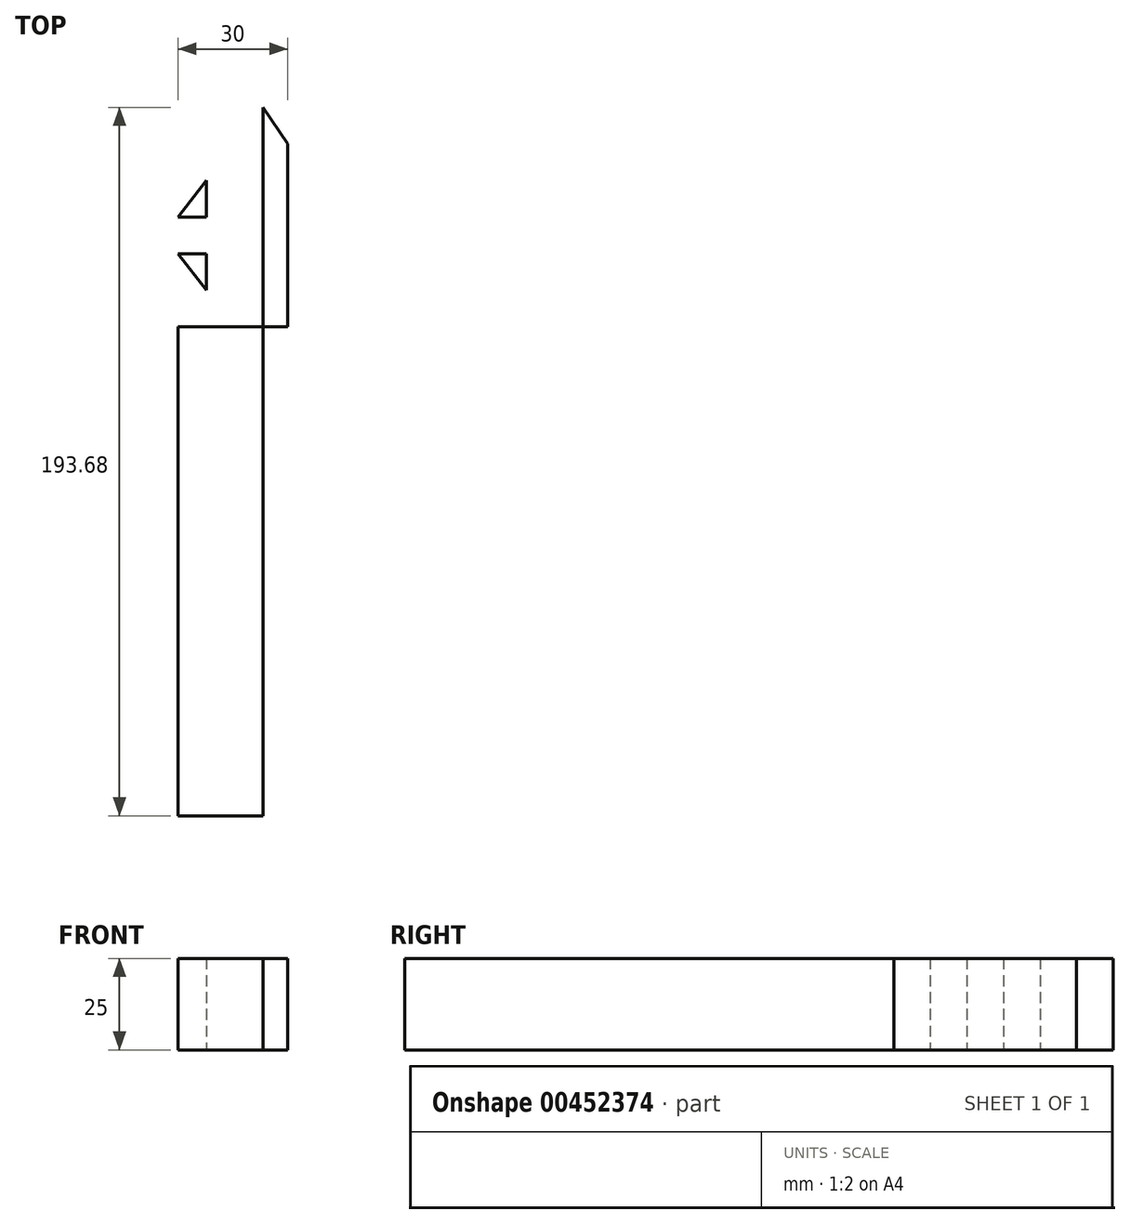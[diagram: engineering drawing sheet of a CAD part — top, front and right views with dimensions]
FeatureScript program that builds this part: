
annotation { "Feature Type Name" : "Feature", "Feature Type Description" : "" }
export const myFeature = defineFeature(function(context is Context, id is Id, definition is map)
    precondition{}
    {
        {
            var Q0;
            Q0=qCreatedBy(makeId("Top.planeOp"),FACE);
            var sketch = newSketch(context, id + "F0", { "sketchPlane" : qUnion([Q0])});
            skLineSegment(sketch, "E0.bottom", {"start": v(-3.87, -96.84) * mm, "end": v(3.87, -96.84) * mm});
            skLineSegment(sketch, "E0.top", {"start": v(-3.87, 96.84) * mm, "end": v(3.87, 96.84) * mm});
            skLineSegment(sketch, "E0.left", {"start": v(-3.87, -96.84) * mm, "end": v(-3.87, 96.84) * mm});
            skLineSegment(sketch, "E0.right", {"start": v(3.87, -96.84) * mm, "end": v(3.87, 96.84) * mm});
            skPoint(sketch, "E0.middle", {"position": v(0, 0) * mm});
            skLineSegment(sketch, "E1.bottom", {"start": v(-3.87, 96.84) * mm, "end": v(-11.62, 96.84) * mm});
            skLineSegment(sketch, "E1.top", {"start": v(-3.87, -96.84) * mm, "end": v(-11.62, -96.84) * mm});
            skLineSegment(sketch, "E1.left", {"start": v(-3.87, 96.84) * mm, "end": v(-3.87, -96.84) * mm});
            skLineSegment(sketch, "E1.right", {"start": v(-11.62, 96.84) * mm, "end": v(-11.62, -96.84) * mm});
            skLineSegment(sketch, "E2.bottom", {"start": v(3.87, -96.84) * mm, "end": v(11.62, -96.84) * mm});
            skLineSegment(sketch, "E2.top", {"start": v(3.87, 96.84) * mm, "end": v(11.62, 96.84) * mm});
            skLineSegment(sketch, "E2.right", {"start": v(11.62, -96.84) * mm, "end": v(11.62, 96.84) * mm});
            skLineSegment(sketch, "E3.bottom", {"start": v(-11.62, 96.84) * mm, "end": v(18.38, 96.84) * mm});
            skLineSegment(sketch, "E3.top", {"start": v(-11.62, 86.84) * mm, "end": v(18.38, 86.84) * mm});
            skLineSegment(sketch, "E3.left", {"start": v(-11.62, 96.84) * mm, "end": v(-11.62, 86.84) * mm});
            skLineSegment(sketch, "E3.right", {"start": v(18.38, 96.84) * mm, "end": v(18.38, 86.84) * mm});
            skLineSegment(sketch, "E4.top", {"start": v(-11.62, 76.84) * mm, "end": v(18.38, 76.84) * mm});
            skLineSegment(sketch, "E4.left", {"start": v(-11.62, 86.84) * mm, "end": v(-11.62, 76.84) * mm});
            skLineSegment(sketch, "E4.right", {"start": v(18.38, 86.84) * mm, "end": v(18.38, 76.84) * mm});
            skLineSegment(sketch, "E5.top", {"start": v(-11.62, 66.84) * mm, "end": v(18.38, 66.84) * mm});
            skLineSegment(sketch, "E5.left", {"start": v(-11.62, 76.84) * mm, "end": v(-11.62, 66.84) * mm});
            skLineSegment(sketch, "E5.right", {"start": v(18.38, 76.84) * mm, "end": v(18.38, 66.84) * mm});
            skLineSegment(sketch, "E6.top", {"start": v(-11.62, 56.84) * mm, "end": v(18.38, 56.84) * mm});
            skLineSegment(sketch, "E6.left", {"start": v(-11.62, 66.84) * mm, "end": v(-11.62, 56.84) * mm});
            skLineSegment(sketch, "E6.right", {"start": v(18.38, 66.84) * mm, "end": v(18.38, 56.84) * mm});
            skLineSegment(sketch, "E7.bottom", {"start": v(-11.62, 56.84) * mm, "end": v(8.73, 56.84) * mm});
            skLineSegment(sketch, "E7.top", {"start": v(-11.62, 46.84) * mm, "end": v(8.73, 46.84) * mm});
            skLineSegment(sketch, "E7.left", {"start": v(-11.62, 56.84) * mm, "end": v(-11.62, 46.84) * mm});
            skLineSegment(sketch, "E8.bottom", {"start": v(-11.62, 46.84) * mm, "end": v(18.38, 46.84) * mm});
            skLineSegment(sketch, "E8.top", {"start": v(-11.62, 36.84) * mm, "end": v(18.38, 36.84) * mm});
            skLineSegment(sketch, "E8.left", {"start": v(-11.62, 46.84) * mm, "end": v(-11.62, 36.84) * mm});
            skLineSegment(sketch, "E8.right", {"start": v(18.38, 46.84) * mm, "end": v(18.38, 36.84) * mm});
            skLineSegment(sketch, "E9", {"start": v(18.38, 56.84) * mm, "end": v(18.38, 46.84) * mm});
            skLineSegment(sketch, "E10", {"start": v(-11.62, 96.84) * mm, "end": v(-3.87, 86.84) * mm});
            skLineSegment(sketch, "E11", {"start": v(-3.87, 86.84) * mm, "end": v(-3.87, 76.84) * mm});
            skLineSegment(sketch, "E12", {"start": v(-3.87, 76.84) * mm, "end": v(-11.62, 66.84) * mm});
            skLineSegment(sketch, "E13", {"start": v(-11.62, 56.84) * mm, "end": v(-3.87, 46.84) * mm});
            skLineSegment(sketch, "E14", {"start": v(11.62, 96.84) * mm, "end": v(18.38, 86.84) * mm});
            skLineSegment(sketch, "E15", {"start": v(18.38, 76.84) * mm, "end": v(11.62, 66.84) * mm});
            skSolve(sketch);
        }
        {
            var Q0;
            {var subQ0=sQuery(id+"F0.wireOp",EDGE,"E1.top");Q0=makeQuery(id+"F0.imprint","IMPRINT",FACE,{"disambiguationData":[TD([[makeQuery(id+"F0.imprint","IMPRINT",EDGE,{"derivedFrom":subQ0}),-1.0]])]});}
            var Q1;
            {var subQ0=sQuery(id+"F0.wireOp",EDGE,"E2.bottom");Q1=makeQuery(id+"F0.imprint","IMPRINT",FACE,{"disambiguationData":[TD([[makeQuery(id+"F0.imprint","IMPRINT",EDGE,{"derivedFrom":subQ0}),1.0]])]});}
            var Q2;
            {var subQ5=sQuery(id+"F0.wireOp",EDGE,"E8.right");Q2=makeQuery(id+"F0.imprint","IMPRINT",FACE,{"disambiguationData":[TD([[makeQuery(id+"F0.imprint","IMPRINT",EDGE,{"derivedFrom":subQ5}),-1.0]])]});}
            var Q3;
            {var subQ0=sQuery(id+"F0.wireOp",EDGE,"E3.left");Q3=makeQuery(id+"F0.imprint","IMPRINT",FACE,{"disambiguationData":[TD([[makeQuery(id+"F0.imprint","IMPRINT",EDGE,{"derivedFrom":subQ0}),1.0]])]});}
            var Q4;
            {var subQ0=sQuery(id+"F0.wireOp",EDGE,"E5.right");Q4=makeQuery(id+"F0.imprint","IMPRINT",FACE,{"disambiguationData":[TD([[makeQuery(id+"F0.imprint","IMPRINT",EDGE,{"derivedFrom":subQ0}),-1.0]])]});}
            var Q5;
            {var subQ0=sQuery(id+"F0.wireOp",EDGE,"E7.left");Q5=makeQuery(id+"F0.imprint","IMPRINT",FACE,{"disambiguationData":[TD([[makeQuery(id+"F0.imprint","IMPRINT",EDGE,{"derivedFrom":subQ0}),1.0]])]});}
            var Q6;
            {var subQ0=sQuery(id+"F0.wireOp",EDGE,"E0.bottom");Q6=makeQuery(id+"F0.imprint","IMPRINT",FACE,{"disambiguationData":[TD([[makeQuery(id+"F0.imprint","IMPRINT",EDGE,{"derivedFrom":subQ0}),1.0]])]});}
            var Q7;
            {var subQ0=sQuery(id+"F0.wireOp",EDGE,"E3.bottom");var subQ5=sQuery(id+"F0.wireOp",EDGE,"E0.right");var subQ6=makeQuery(id+"F0.imprint","INTERSECT",VERTEX,{"derivedFrom":[subQ5,subQ0]});Q7=makeQuery(id+"F0.imprint","IMPRINT",FACE,{"disambiguationData":[TD([[makeQuery(id+"F0.imprint","IMPRINT",EDGE,{"disambiguationData":[TD([[subQ6,1.0]])],"derivedFrom":subQ5}),1.0]])]});}
            var Q8;
            {var subQ5=sQuery(id+"F0.wireOp",EDGE,"E6.left");Q8=makeQuery(id+"F0.imprint","IMPRINT",FACE,{"disambiguationData":[TD([[makeQuery(id+"F0.imprint","IMPRINT",EDGE,{"derivedFrom":subQ5}),1.0]])]});}
            var Q9;
            {var subQ0=sQuery(id+"F0.wireOp",EDGE,"E13");Q9=makeQuery(id+"F0.imprint","IMPRINT",FACE,{"disambiguationData":[TD([[makeQuery(id+"F0.imprint","IMPRINT",EDGE,{"derivedFrom":subQ0}),1.0]])]});}
            var Q10;
            {var subQ5=sQuery(id+"F0.wireOp",EDGE,"E8.left");Q10=makeQuery(id+"F0.imprint","IMPRINT",FACE,{"disambiguationData":[TD([[makeQuery(id+"F0.imprint","IMPRINT",EDGE,{"derivedFrom":subQ5}),1.0]])]});}
            var Q11;
            {var subQ0=sQuery(id+"F0.wireOp",EDGE,"E3.bottom");var subQ1=sQuery(id+"F0.wireOp",EDGE,"E0.right");var subQ2=makeQuery(id+"F0.imprint","INTERSECT",VERTEX,{"derivedFrom":[subQ1,subQ0]});Q11=makeQuery(id+"F0.imprint","IMPRINT",FACE,{"disambiguationData":[TD([[makeQuery(id+"F0.imprint","IMPRINT",EDGE,{"disambiguationData":[TD([[subQ2,1.0]])],"derivedFrom":subQ1}),-1.0]])]});}
            var Q12;
            {var subQ5=sQuery(id+"F0.wireOp",EDGE,"E9");Q12=makeQuery(id+"F0.imprint","IMPRINT",FACE,{"disambiguationData":[TD([[makeQuery(id+"F0.imprint","IMPRINT",EDGE,{"derivedFrom":subQ5}),-1.0]])]});}
            var Q13;
            {var subQ5=sQuery(id+"F0.wireOp",EDGE,"E6.right");Q13=makeQuery(id+"F0.imprint","IMPRINT",FACE,{"disambiguationData":[TD([[makeQuery(id+"F0.imprint","IMPRINT",EDGE,{"derivedFrom":subQ5}),-1.0]])]});}
            var Q14;
            {var subQ0=sQuery(id+"F0.wireOp",EDGE,"E15");Q14=makeQuery(id+"F0.imprint","IMPRINT",FACE,{"disambiguationData":[TD([[makeQuery(id+"F0.imprint","IMPRINT",EDGE,{"derivedFrom":subQ0}),-1.0]])]});}
            var Q15;
            {var subQ5=sQuery(id+"F0.wireOp",EDGE,"E4.right");Q15=makeQuery(id+"F0.imprint","IMPRINT",FACE,{"disambiguationData":[TD([[makeQuery(id+"F0.imprint","IMPRINT",EDGE,{"derivedFrom":subQ5}),-1.0]])]});}
            var Q16;
            {var subQ0=sQuery(id+"F0.wireOp",EDGE,"E14");Q16=makeQuery(id+"F0.imprint","IMPRINT",FACE,{"disambiguationData":[TD([[makeQuery(id+"F0.imprint","IMPRINT",EDGE,{"derivedFrom":subQ0}),-1.0]])]});}
            var Q17;
            {var subQ0=sQuery(id+"F0.wireOp",EDGE,"E4.left");Q17=makeQuery(id+"F0.imprint","IMPRINT",FACE,{"disambiguationData":[TD([[makeQuery(id+"F0.imprint","IMPRINT",EDGE,{"derivedFrom":subQ0}),1.0]])]});}
            var Q18;
            {var subQ0=sQuery(id+"F0.wireOp",EDGE,"E8.bottom");var subQ1=makeQuery(id+"F0.imprint","IMPRINT",VERTEX,{"derivedFrom":subQ0});Q18=makeQuery(id+"F0.imprint","IMPRINT",FACE,{"disambiguationData":[TD([[makeQuery(id+"F0.imprint","IMPRINT",EDGE,{"disambiguationData":[TD([[subQ1,1.0]])],"derivedFrom":subQ0}),-1.0]])]});}
            var Q19;
            {var subQ0=sQuery(id+"F0.wireOp",EDGE,"E12");Q19=makeQuery(id+"F0.imprint","IMPRINT",FACE,{"disambiguationData":[TD([[makeQuery(id+"F0.imprint","IMPRINT",EDGE,{"derivedFrom":subQ0}),1.0]])]});}
            extrude(context, id + "F1", {"entities" : qUnion([Q0, Q1, Q2, Q3, Q4, Q5, Q6, Q7, Q8, Q9, Q10, Q11, Q12, Q13, Q14, Q15, Q16, Q17, Q18, Q19]), "depth" : 25 * mm});
        }
    });
